# Revit family: TTH225
name_source: partatom
category: Generic Models
revit_build: Autodesk Revit LT 2017 (Build: 20160225_1515(x64)
units: mm (PartAtom-declared; Revit-internal decimal feet)

## family parameters
Always vertical = No
Can host rebar = No
Cut with Voids When Loaded = No
Part Type = Normal
Room Calculation Point = No
Round Connector Dimension = Use Diameter
Shared = No
Work Plane-Based = Yes

## types (1)
- NBS Standard Parameters
    BIMObjectName = Role_Source_Type_Generic
    Default Elevation = 1219 mm
    Description = TTH225 -225mm Tray Hanger
    DurationUnit = year
    Finish = Pre Galvanised
    Keynote = Compliant to LU  standard 1-085
    ManufacturerName = Metpro Ltd
    ManufacturerURL = www.metpro.co.uk
    Material = Pre Galvanised Steel
    ModelReference = TTH225
    NBSDescription = Cable Trunking
    NBSReference = 90-55-10/410
    NominalHeight = 240 mm  [stored 0.787402 ft]
    NominalLength = 280 mm  [stored 0.918635 ft]
    NominalWidth = 65 mm  [stored 0.213255 ft]
    Size = 225
    Uniclass2 = PR_65_70_11_18
    Version = 1
    WarrantyDurationUnit = year
    Weight = 0.490Kg

note: [stored X ft] marks values corroborated as IEEE doubles in the binary element streams (Revit-internal decimal feet)

## geometry (parser evidence)
native form markers: Sweep x2
no freeform markers — native parametric forms only
